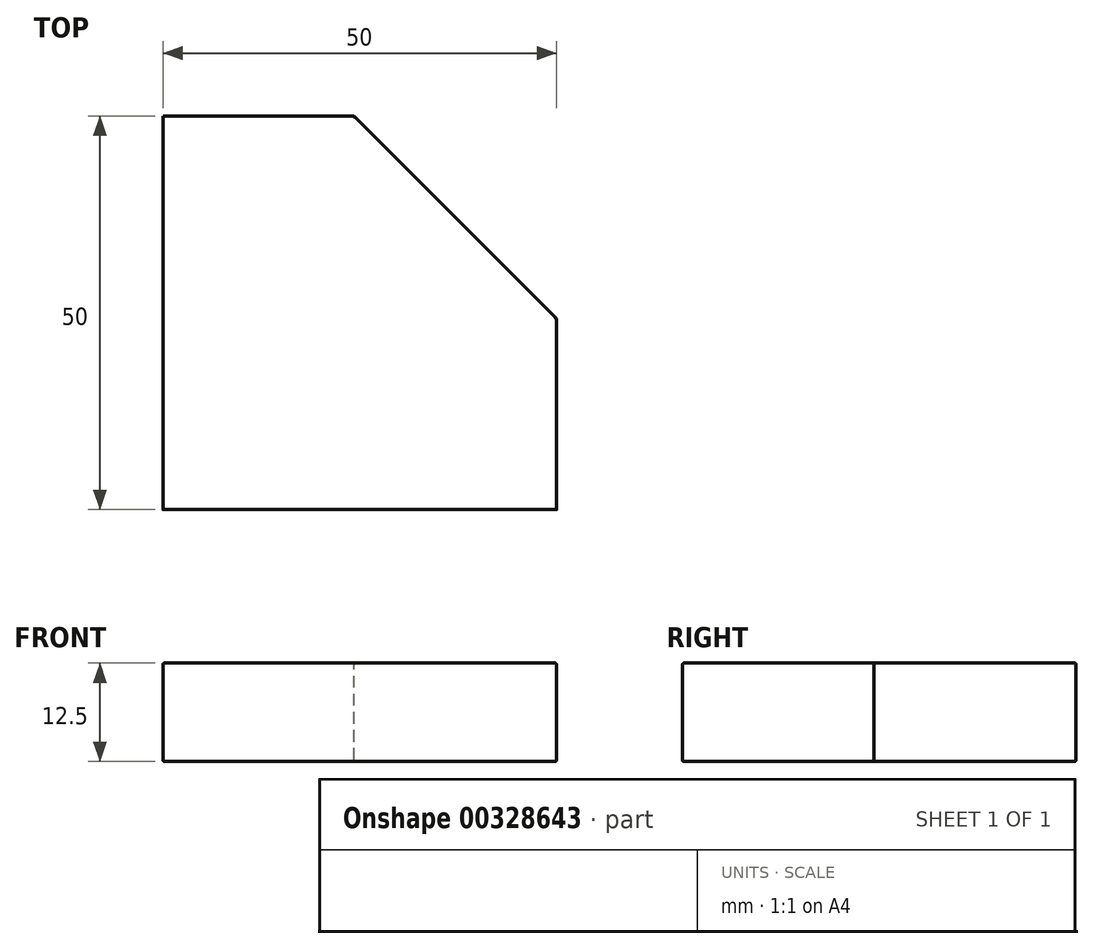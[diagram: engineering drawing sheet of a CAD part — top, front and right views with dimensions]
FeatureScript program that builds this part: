
annotation { "Feature Type Name" : "Feature", "Feature Type Description" : "" }
export const myFeature = defineFeature(function(context is Context, id is Id, definition is map)
    precondition{}
    {
        {
            var Q0;
            Q0=qCreatedBy(makeId("Top.planeOp"),FACE);
            var sketch = newSketch(context, id + "F0", { "sketchPlane" : qUnion([Q0])});
            skLineSegment(sketch, "E0.bottom", {"start": v(0, 0) * mm, "end": v(50, 0) * mm});
            skLineSegment(sketch, "E0.top", {"start": v(0, 50) * mm, "end": v(24.3, 50) * mm});
            skLineSegment(sketch, "E0.left", {"start": v(0, 0) * mm, "end": v(0, 50) * mm});
            skLineSegment(sketch, "E0.right", {"start": v(50, 0) * mm, "end": v(50, 24.3) * mm});
            skLineSegment(sketch, "E1", {"start": v(50, 24.3) * mm, "end": v(24.3, 50) * mm});
            skSolve(sketch);
        }
        {
            var Q0;
            Q0=qSketchRegion(id+"F0",true);
            extrude(context, id + "F1", {"entities" : qUnion([Q0]), "oppositeDirection" : true, "depth" : 12.5 * mm});
        }
        {
            var Q0;
            Q0=makeQuery(id+"F1.opExtrude","CAP_FACE",FACE,{"disambiguationData":[OSD([sQuery(id+"F0.wireOp",EDGE,"E0.bottom"),sQuery(id+"F0.wireOp",EDGE,"E0.top"),sQuery(id+"F0.wireOp",EDGE,"E0.left"),sQuery(id+"F0.wireOp",EDGE,"E0.right")])],"isStart":true});
            var Q1;
            Q1=makeQuery(id+"F1.opExtrude","CAP_FACE",FACE,{"disambiguationData":[OSD([sQuery(id+"F0.wireOp",EDGE,"E0.bottom"),sQuery(id+"F0.wireOp",EDGE,"E0.top"),sQuery(id+"F0.wireOp",EDGE,"E0.left"),sQuery(id+"F0.wireOp",EDGE,"E0.right")])],"isStart":false});
            fillet(context, id + "F2", {"entities" : qUnion([Q0, Q1]), "radius" : .2 * mm, "tangentPropagation" : true, "allowEdgeOverflow" : false});
        }
    });
